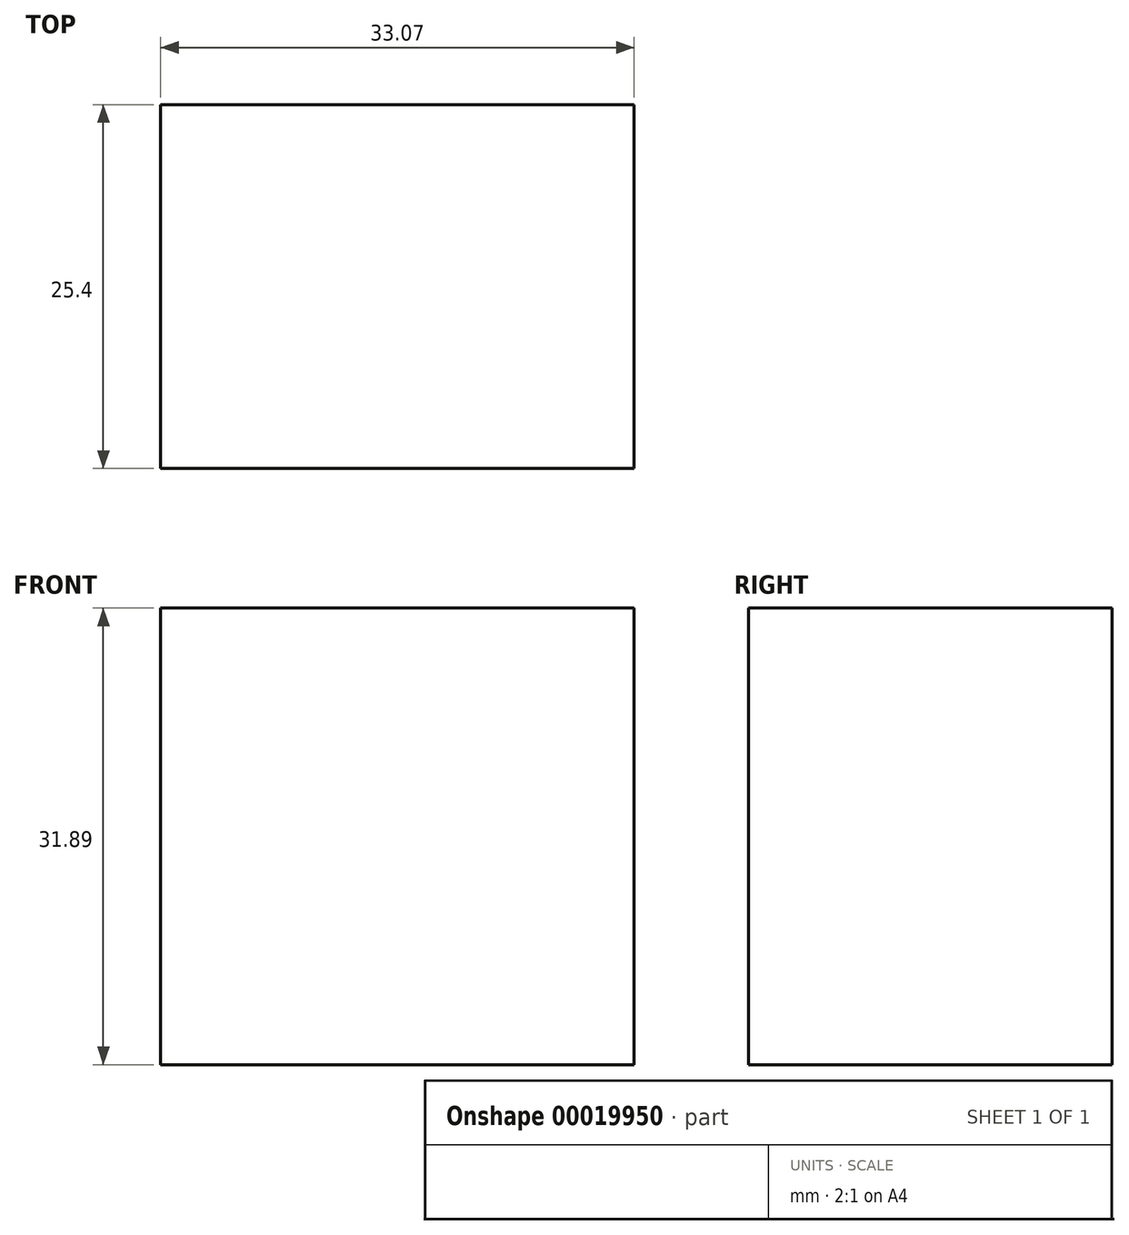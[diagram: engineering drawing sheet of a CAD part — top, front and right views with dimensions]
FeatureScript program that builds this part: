
annotation { "Feature Type Name" : "Feature", "Feature Type Description" : "" }
export const myFeature = defineFeature(function(context is Context, id is Id, definition is map)
    precondition{}
    {
        {
            var Q0;
            Q0=qCreatedBy(makeId("Front.planeOp"),FACE);
            var sketch = newSketch(context, id + "F0", { "sketchPlane" : qUnion([Q0])});
            skLineSegment(sketch, "E0.bottom", {"start": v(-48.27, 34.72) * mm, "end": v(39.33, 34.72) * mm});
            skLineSegment(sketch, "E0.top", {"start": v(-48.27, -38) * mm, "end": v(39.33, -38) * mm});
            skLineSegment(sketch, "E0.left", {"start": v(-48.27, 34.72) * mm, "end": v(-48.27, -38) * mm});
            skLineSegment(sketch, "E0.right", {"start": v(39.33, 34.72) * mm, "end": v(39.33, -38) * mm});
            skLineSegment(sketch, "E1.bottom", {"start": v(-48.27, 34.72) * mm, "end": v(-15.2, 34.72) * mm});
            skLineSegment(sketch, "E1.top", {"start": v(-48.27, 2.83) * mm, "end": v(-15.2, 2.83) * mm});
            skLineSegment(sketch, "E1.left", {"start": v(-48.27, 34.72) * mm, "end": v(-48.27, 2.83) * mm});
            skLineSegment(sketch, "E1.right", {"start": v(-15.2, 34.72) * mm, "end": v(-15.2, 2.83) * mm});
            skSolve(sketch);
        }
        {
            var Q0;
            Q0=makeQuery(id+"F0.imprint","IMPRINT",FACE,{"disambiguationData":[TD([[makeQuery(id+"F0.imprint","IMPRINT",EDGE,{"derivedFrom":sQuery(id+"F0.wireOp",EDGE,"E0.bottom")}),-1.0]])]});
            extrude(context, id + "F1", {"entities" : qUnion([Q0]), "depth" : 25.4 * mm});
        }
    });
